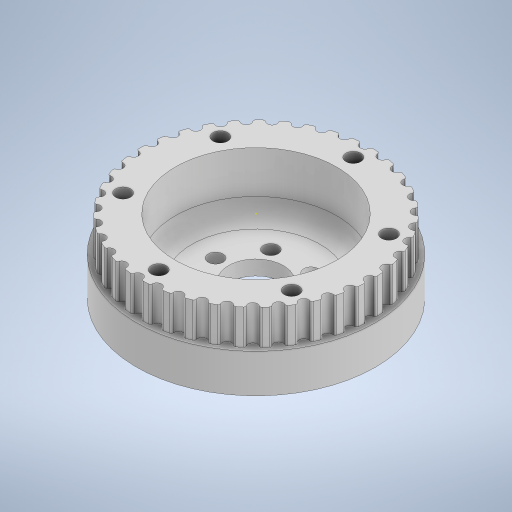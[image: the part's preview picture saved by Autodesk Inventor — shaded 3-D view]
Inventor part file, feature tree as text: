
AUTODESK INVENTOR PART (.ipt)
format: ipt  version: 2024 (Build 280153000, 153)  size: 672,256 bytes
history: native  units: mm
features: sketch x11, extrude x10, projected_geometry x4, fillet x2, pattern_circular x1
ambient origin geometry x8: Origin, YZ Plane, XZ Plane, XY Plane, X Axis, Y Axis, Z Axis, Center Point
bodies: Solid1 (feature_tree)
feature tree (28):
  extrude  "Extrusion1"  Depth=106.0mm
  extrude  "Extrusion2"  Depth=8.0mm TaperAngle=0.0deg
  extrude  "Extrusion3"  Depth=8.0mm TaperAngle=0.0deg
  extrude  "Extrusion4"  Depth=8.1mm
  extrude  "Extrusion5"  Depth=60.0mm
  extrude  "Extrusion6"  Depth=20.0mm TaperAngle=0.0deg
  extrude  "Extrusion7"  Depth=93.5mm
  extrude  "Extrusion8"  Depth=22.0mm TaperAngle=0.0deg
  extrude  "Extrusion9"  Depth=32.0mm TaperAngle=0.0deg
  pattern_circular  "Circular Pattern1"  Count=39 Angle=360.0deg
  fillet  "Fillet1"  Radius=9.0mm
  extrude  "Extrusion10"  Depth=1.0mm
  fillet  "Fillet2"  Radius=130.0mm
  sketch  "Sketch11"  dims[d39=5.1mm d40=125.0mm d41=130.0mm d42=21.0mm d43=0.0mm d44=61.9mm d45=1.0mm]
  sketch  "Sketch1"  dims[d0=125.0mm d1=106.0mm]
  sketch  "Sketch2"  dims[d2=60.0mm d4=360.0deg d6=8.0mm d7=0.0mm]
  sketch  "Sketch3"  dims[d8=30.0mm d9=8.0mm d10=0.0mm]
  projected_geometry  "Projected Loop1"
  sketch  "Sketch4"  dims[d11=22.0mm d12=8.1mm]
  projected_geometry  "Projected Loop2"
  sketch  "Sketch5"  dims[d13=60.0mm d15=360.0deg d17=60.0mm]
  projected_geometry  "Projected Loop3"
  sketch  "Sketch6"  dims[d18=8.1mm d19=20.0mm d20=0.0mm]
  sketch  "Sketch7"  dims[d22=7.0mm d23=0.0mm d24=93.5mm]
  projected_geometry  "Projected Loop4"
  sketch  "Sketch8"  dims[d25=2.0mm d26=0.0mm d27=22.0mm d28=0.0mm]
  sketch  "Sketch9"  dims[d29=32.0mm d30=0.0mm d31=32.0mm d32=0.0mm]
  sketch  "Sketch10"  dims[d33=19.0mm d34=0.0mm d35=390.0mm d36=360.0deg d38=9.0mm]
